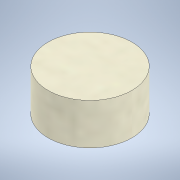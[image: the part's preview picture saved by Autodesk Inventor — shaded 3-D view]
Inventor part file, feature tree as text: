
AUTODESK INVENTOR PART (.ipt)
format: ipt  version: 2021 (Build 250183000, 183)  size: 100,864 bytes
history: native  units: mm
features: extrude x1, sketch x1
ambient origin geometry x8: Origin, YZ Plane, XZ Plane, XY Plane, X Axis, Y Axis, Z Axis, Center Point
bodies: Solid1 (feature_tree)
feature tree (2):
  extrude  "Extrusion1"  Depth=12.4mm TaperAngle=0.0deg
  sketch  "Sketch1"  dims[d0=25.25mm d1=12.4mm d2=0.0mm]
